# Revit family: Temper_83_КранШаровый-ВН_Рычаг_GAS
name_source: partatom
category: Арматура трубопроводов
units: mm (PartAtom-declared; Revit-internal decimal feet)

## family parameters
Всегда вертикально = Да
На основе рабочей плоскости = Нет
Общий = Нет
При загрузке вырезать с полостями = Нет
Размер круглого соединителя = Использовать диаметр
Тип детали = Вставляется

## types (6) — shared parameters
ADSK_URL документации изделия = https://brass.temper.ru
ADSK_URL страницы изделия = https://brass.temper.ru
ADSK_Версия Revit = 2019
ADSK_Версия семейства = v1.0
ADSK_Единица измерения = шт.
ADSK_Завод-изготовитель = ООО «ТД «Темпер»
ADSK_Количество = 1
ADSK_Материал = Латунь ЛС59-1В
ADSK_Наименование краткое = Кран шаровой латунный Temper
ADSK_Обозначение = ГОСТ Р 59553-2021
N = 4
Изготовитель = ООО «ТД «Темпер»
Разработчик = https://3dbim.pro
ТВ = ВН
ТВ1 = temper

## per-type parameters (varying)
| type | ADSK_Диаметр условный | ADSK_Код изделия | ADSK_Марка | ADSK_Масса | ADSK_Масса_Текст | ADSK_Наименование |
| DN 15 | 15 мм | 8315ВНР1240 | 8315ВНР1240 | 0.161 | 0.161 | Кран шаровый латунный Temper для газа DN15 (12”) PN40 внутренняянаружная рычаг GAS |
| DN 20 | 20 мм | 8320ВНР3440 | 8320ВНР3440 | 0.216 | 0.216 | Кран шаровый латунный Temper для газа  DN20 (34”) PN40 внутренняянаружная рычаг GAS |
| DN 50 | 50 мм | 8350ВНР225 | 8350ВНР225 | 1.54 | 1.54 | Кран шаровый латунный Temper для газа DN50 (2”) PN25 внутренняянаружная рычаг GAS |
| DN 40 | 40 мм | 8340ВНР11225 | 8340ВНР11225 | 0.957 | 0.957 | Кран шаровый латунный Temper для газа DN40 (1.12”) PN25 внутренняянаружная рычаг GAS |
| DN 32 | 32 мм | 8332ВНР11425 | 8332ВНР11425 | 0.64 | 0.64 | Кран шаровый латунный Temper для газа DN32 (1.14”) PN25 внутренняянаружная рычаг GAS |
| DN 25 | 25 мм | 8325ВНР140 | 8325ВНР140 | 0.323 | 0.323 | Кран шаровый латунный Temper для газа  DN25 (1”) PN40 внутренняянаружная рычаг GAS |
